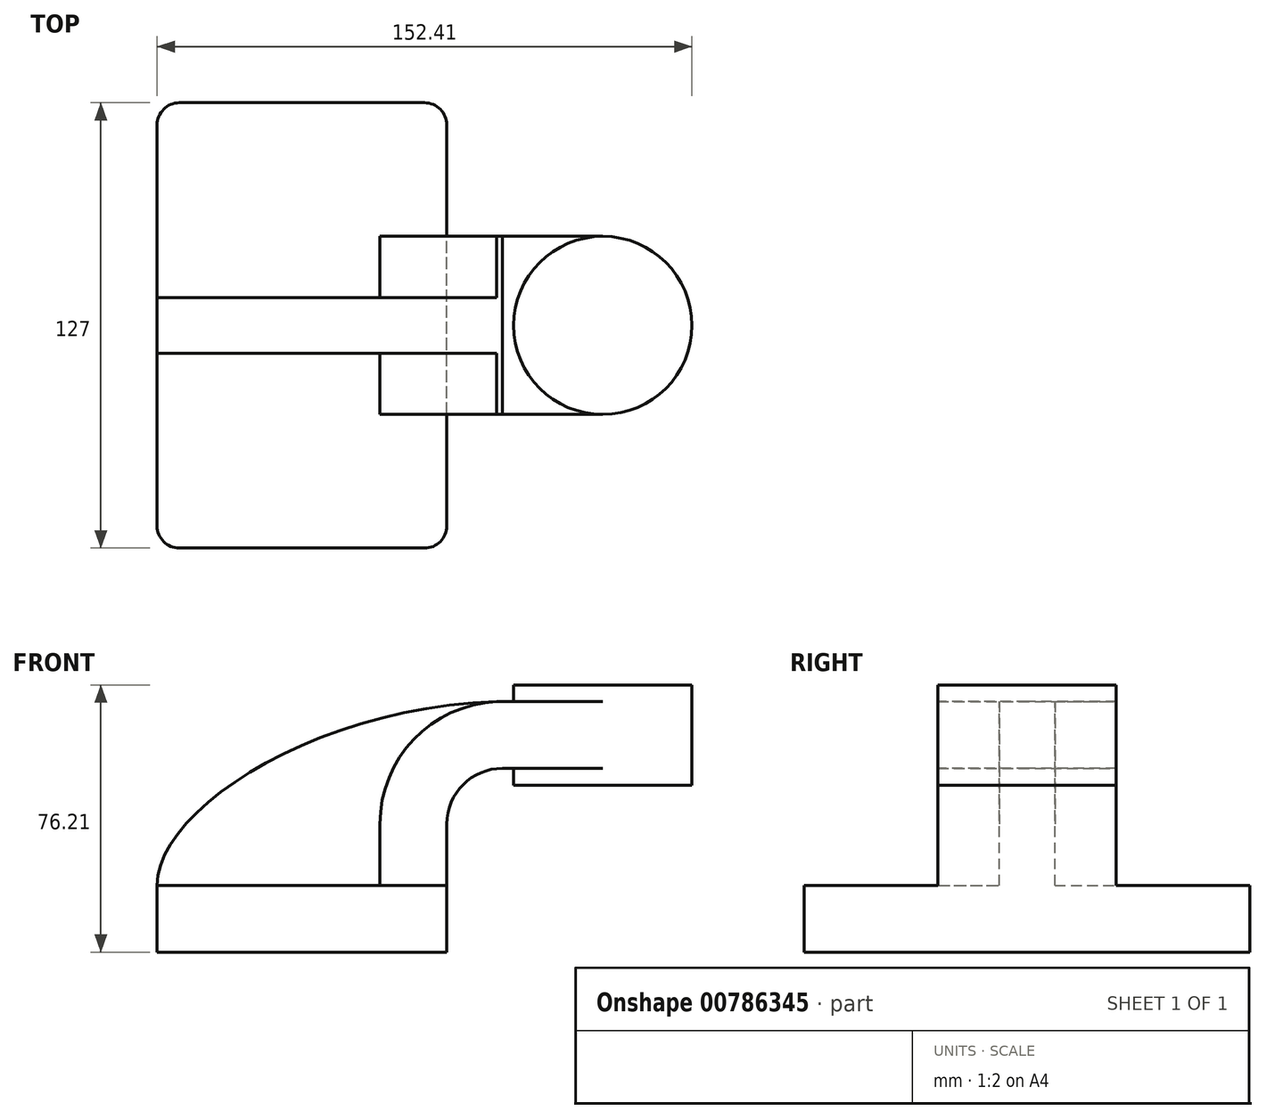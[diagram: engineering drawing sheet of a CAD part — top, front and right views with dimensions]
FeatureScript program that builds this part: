
annotation { "Feature Type Name" : "Feature", "Feature Type Description" : "" }
export const myFeature = defineFeature(function(context is Context, id is Id, definition is map)
    precondition{}
    {
        {
            var Q0;
            Q0=qCreatedBy(makeId("Front.planeOp"),FACE);
            var sketch = newSketch(context, id + "F0", { "sketchPlane" : qUnion([Q0])});
            skLineSegment(sketch, "E0.bottom", {"start": v(41.27, 9.53) * mm, "end": v(-41.28, 9.53) * mm});
            skLineSegment(sketch, "E0.top", {"start": v(41.28, -9.52) * mm, "end": v(-41.27, -9.52) * mm});
            skLineSegment(sketch, "E0.left", {"start": v(41.28, 9.53) * mm, "end": v(41.28, -9.52) * mm});
            skLineSegment(sketch, "E0.right", {"start": v(-41.28, 9.53) * mm, "end": v(-41.28, -9.52) * mm});
            skPoint(sketch, "E0.middle", {"position": v(0, 0) * mm});
            skLineSegment(sketch, "E1", {"start": v(41.27, 9.53) * mm, "end": v(41.27, 27) * mm});
            skLineSegment(sketch, "E2.bottom", {"start": v(60.32, 38.1) * mm, "end": v(111.12, 38.1) * mm});
            skLineSegment(sketch, "E2.top", {"start": v(60.32, 66.68) * mm, "end": v(111.12, 66.68) * mm});
            skLineSegment(sketch, "E2.left", {"start": v(60.32, 38.1) * mm, "end": v(60.32, 66.68) * mm});
            skLineSegment(sketch, "E2.right", {"start": v(111.12, 38.1) * mm, "end": v(111.12, 66.68) * mm});
            skPoint(sketch, "E2.middle", {"position": v(85.72, 52.39) * mm});
            skArc(sketch, "E3", {"start": v(41.27, 27) * mm, "mid": v(45.92, 38.23) * mm, "end": v(57.15, 42.88) * mm});
            skLineSegment(sketch, "E4", {"start": v(57.15, 42.88) * mm, "end": v(85.72, 42.88) * mm});
            skPoint(sketch, "E4.endSnap0", {"position": v(85.72, 38.1) * mm});
            skLineSegment(sketch, "E5.0", {"start": v(57.15, 61.93) * mm, "end": v(85.72, 61.93) * mm});
            skArc(sketch, "E5.1", {"start": v(22.22, 27) * mm, "mid": v(32.45, 51.7) * mm, "end": v(57.15, 61.93) * mm});
            skLineSegment(sketch, "E5.2", {"start": v(22.22, 9.53) * mm, "end": v(22.22, 27) * mm});
            skLineSegment(sketch, "E6", {"start": v(85.72, 38.1) * mm, "end": v(85.72, 66.68) * mm});
            skFitSpline(sketch, "E7", {"points": [v(-41.28, 9.52) * mm, v(57.15, 61.93) * mm], "startDerivative": vector(0.03, 64.38) * mm, "endDerivative": vector(159.88, 2.87) * mm});
            skSolve(sketch);
        }
        {
            var Q0;
            Q0=makeQuery(id+"F0.imprint","IMPRINT",FACE,{"disambiguationData":[TD([[makeQuery(id+"F0.imprint","IMPRINT",EDGE,{"derivedFrom":sQuery(id+"F0.wireOp",EDGE,"E0.top")}),-1.0]])]});
            extrude(context, id + "F1", {"entities" : qUnion([Q0]), "endBound" : BoundingType.SYMMETRIC, "depth" : 127 * mm, "offsetDistance" : 25.4 * mm});
        }
        {
            var Q0;
            {var subQ6=sQuery(id+"F0.wireOp",EDGE,"E1");Q0=makeQuery(id+"F0.imprint","IMPRINT",FACE,{"disambiguationData":[TD([[makeQuery(id+"F0.imprint","IMPRINT",EDGE,{"derivedFrom":subQ6}),1.0]])]});}
            var Q1;
            {var subQ0=sQuery(id+"F0.wireOp",EDGE,"E4");var subQ1=sQuery(id+"F0.wireOp",EDGE,"E2.left");var subQ2=makeQuery(id+"F0.imprint","INTERSECT",VERTEX,{"derivedFrom":[subQ1,subQ0]});Q1=makeQuery(id+"F0.imprint","IMPRINT",FACE,{"disambiguationData":[TD([[makeQuery(id+"F0.imprint","IMPRINT",EDGE,{"disambiguationData":[TD([[subQ2,-1.0]])],"derivedFrom":subQ1}),-1.0]])]});}
            extrude(context, id + "F2", {"entities" : qUnion([Q0, Q1]), "operationType" : NewBodyOperationType.ADD, "endBound" : BoundingType.SYMMETRIC, "depth" : 50.8 * mm, "offsetDistance" : 25.4 * mm});
        }
        {
            var Q0;
            {var subQ3=sQuery(id+"F0.wireOp",EDGE,"E5.2");Q0=makeQuery(id+"F0.imprint","IMPRINT",FACE,{"disambiguationData":[TD([[makeQuery(id+"F0.imprint","IMPRINT",EDGE,{"derivedFrom":subQ3}),1.0]])]});}
            extrude(context, id + "F3", {"entities" : qUnion([Q0]), "operationType" : NewBodyOperationType.ADD, "endBound" : BoundingType.SYMMETRIC, "depth" : 15.88 * mm, "offsetDistance" : 25.4 * mm});
        }
        {
            var Q0;
            {var subQ0=sQuery(id+"F0.wireOp",EDGE,"E2.right");Q0=makeQuery(id+"F0.imprint","IMPRINT",FACE,{"disambiguationData":[TD([[makeQuery(id+"F0.imprint","IMPRINT",EDGE,{"derivedFrom":subQ0}),1.0]])]});}
            var Q1;
            Q1=sQuery(id+"F0.wireOp",EDGE,"E6");
            revolve(context, id + "F4", {"operationType" : NewBodyOperationType.ADD, "surfaceOperationType" : NewSurfaceOperationType.NEW, "entities" : qUnion([Q0]), "axis" : qUnion([Q1]), "revolveType" : RevolveType.FULL});
        }
        {
            var Q0;
            Q0=makeQuery(id+"F1.opExtrude","CAP_EDGE",EDGE,{"disambiguationData":[OSD([sQuery(id+"F0.wireOp",EDGE,"E0.right")])],"isStart":false});
            var Q1;
            Q1=makeQuery(id+"F1.opExtrude","CAP_EDGE",EDGE,{"disambiguationData":[OSD([sQuery(id+"F0.wireOp",EDGE,"E0.left")])],"isStart":false});
            var Q2;
            Q2=makeQuery(id+"F1.opExtrude","CAP_EDGE",EDGE,{"disambiguationData":[OSD([sQuery(id+"F0.wireOp",EDGE,"E0.left")])],"isStart":true});
            var Q3;
            Q3=makeQuery(id+"F1.opExtrude","CAP_EDGE",EDGE,{"disambiguationData":[OSD([sQuery(id+"F0.wireOp",EDGE,"E0.right")])],"isStart":true});
            fillet(context, id + "F5", {"entities" : qUnion([Q0, Q1, Q2, Q3]), "radius" : 6.35 * mm, "tangentPropagation" : true, "allowEdgeOverflow" : false});
        }
    });
